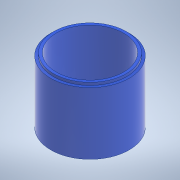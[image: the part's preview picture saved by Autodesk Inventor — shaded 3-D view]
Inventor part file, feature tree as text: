
AUTODESK INVENTOR PART (.ipt)
format: ipt  version: 2020 (Build 240168000, 168)  size: 131,584 bytes
history: native  units: mm
features: extrude x2, sketch x1
ambient origin geometry x8: Origin, YZ Plane, XZ Plane, XY Plane, X Axis, Y Axis, Z Axis, Center Point
bodies: Solid1 (feature_tree)
feature tree (3):
  sketch  "Sketch1"  dims[d0=100.0mm d1=108.0mm d2=116.0mm d3=92.0mm d4=0.0mm d5=88.0mm d6=4.0mm d7=0.0mm d8=0.0mm]
  extrude  "Extrusion1"  Depth=4.0mm
  extrude  "Extrusion2"  Depth=4.0mm
